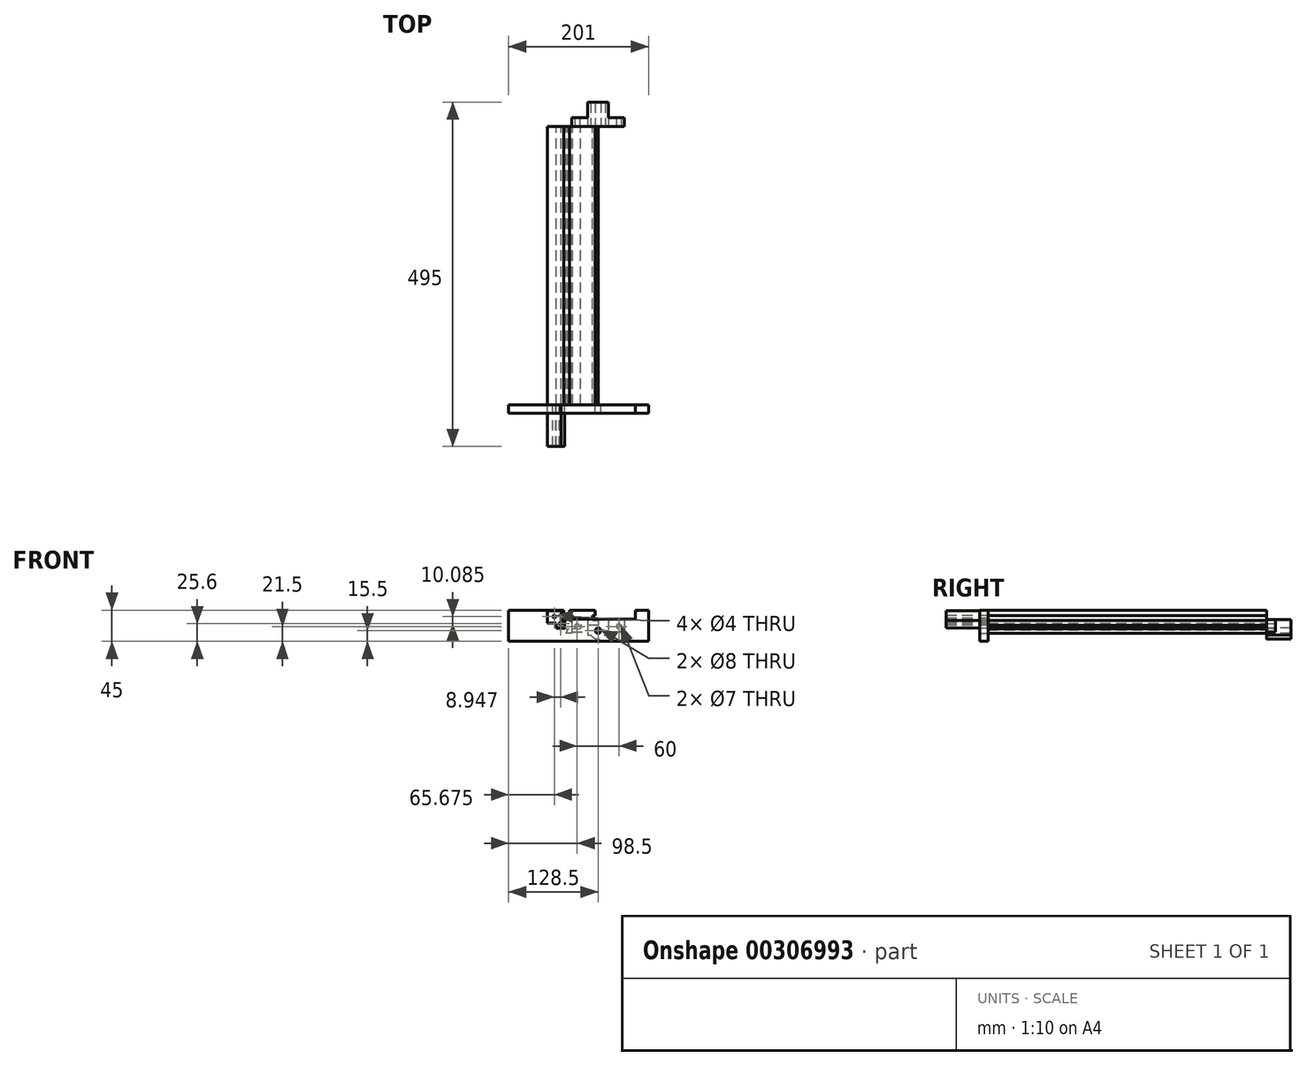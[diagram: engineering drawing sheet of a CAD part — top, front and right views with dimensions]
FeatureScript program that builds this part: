
annotation { "Feature Type Name" : "Feature", "Feature Type Description" : "" }
export const myFeature = defineFeature(function(context is Context, id is Id, definition is map)
    precondition{}
    {
        {
            var Q0;
            Q0=qCreatedBy(makeId("Front.planeOp"),FACE);
            var sketch = newSketch(context, id + "F0", { "sketchPlane" : qUnion([Q0])});
            skLineSegment(sketch, "E0", {"start": v(-4, 13.5) * mm, "end": v(-4, 5.5) * mm});
            skLineSegment(sketch, "E1", {"start": v(-4, 5.5) * mm, "end": v(-8.15, 5.5) * mm});
            skLineSegment(sketch, "E2", {"start": v(-8.15, 5.5) * mm, "end": v(-8.15, -1.5) * mm});
            skLineSegment(sketch, "E3", {"start": v(-8.15, -1.5) * mm, "end": v(0, -1.5) * mm});
            skLineSegment(sketch, "E4.MirrorCS", {"start": v(-45, 13.5) * mm, "end": v(-45, 30.96) * mm, "construction": true});
            skLineSegment(sketch, "E5.trimOffspring", {"start": v(-49, 13.5) * mm, "end": v(-72.5, 13.5) * mm});
            skLineSegment(sketch, "E6", {"start": v(-59.88, -5.13) * mm, "end": v(-59.88, -13.5) * mm});
            skLineSegment(sketch, "E7", {"start": v(-59.88, -13.5) * mm, "end": v(-43.75, -13.5) * mm});
            skLineSegment(sketch, "E8", {"start": v(-43.8, -14.95) * mm, "end": v(-46.06, -18.88) * mm});
            skLineSegment(sketch, "E9.0", {"start": v(-38.1, -19.88) * mm, "end": v(-46.06, -19.88) * mm});
            skLineSegment(sketch, "E10", {"start": v(-38.1, -13.32) * mm, "end": v(-38.1, -19.88) * mm});
            skLineSegment(sketch, "E11.MirrorCS", {"start": v(-43.75, -13.5) * mm, "end": v(-43.05, -12.8) * mm});
            skLineSegment(sketch, "E12.0", {"start": v(-43.8, -14.95) * mm, "end": v(-42.34, -13.5) * mm});
            skLineSegment(sketch, "E13", {"start": v(-42.34, -13.5) * mm, "end": v(-43.05, -12.8) * mm});
            skLineSegment(sketch, "E14", {"start": v(-46.06, -18.88) * mm, "end": v(-46.06, -19.88) * mm});
            skPoint(sketch, "E15.end.orphan", {"position": v(38.1, -8.38) * mm});
            skLineSegment(sketch, "E16", {"start": v(0, -8.5) * mm, "end": v(-25, -8.5) * mm});
            skLineSegment(sketch, "E17", {"start": v(-25, -8.5) * mm, "end": v(-25, -13.09) * mm});
            skLineSegment(sketch, "E18", {"start": v(-48.57, -13.5) * mm, "end": v(-42.45, -13.4) * mm, "construction": true});
            skLineSegment(sketch, "E19.trimOffspring", {"start": v(-38.1, -13.32) * mm, "end": v(-25, -13.09) * mm});
            skLineSegment(sketch, "E20.0", {"start": v(-49, -13.5) * mm, "end": v(-59.88, -13.5) * mm});
            skLineSegment(sketch, "E21", {"start": v(-72.5, 13.5) * mm, "end": v(-72.5, -5.13) * mm});
            skLineSegment(sketch, "E22", {"start": v(-72.5, -5.13) * mm, "end": v(-59.88, -5.13) * mm});
            skLineSegment(sketch, "E23.0.1.0", {"start": v(-53.15, -1.5) * mm, "end": v(-45, -1.5) * mm});
            skLineSegment(sketch, "E23.1.1.0", {"start": v(-49, 13.5) * mm, "end": v(-49, 5.5) * mm});
            skLineSegment(sketch, "E23.2.1.0", {"start": v(-49, 5.5) * mm, "end": v(-53.15, 5.5) * mm});
            skLineSegment(sketch, "E23.3.1.0", {"start": v(-53.15, 5.5) * mm, "end": v(-53.15, -1.5) * mm});
            skLineSegment(sketch, "E24.MirrorCS", {"start": v(-36.85, 5.5) * mm, "end": v(-36.85, -1.5) * mm});
            skLineSegment(sketch, "E25.MirrorCS", {"start": v(-41, 13.5) * mm, "end": v(-41, 5.5) * mm});
            skLineSegment(sketch, "E26.MirrorCS", {"start": v(-41, 5.5) * mm, "end": v(-36.85, 5.5) * mm});
            skLineSegment(sketch, "E27.MirrorCS", {"start": v(-36.85, -1.5) * mm, "end": v(-45, -1.5) * mm});
            skLineSegment(sketch, "E28", {"start": v(-41, 13.5) * mm, "end": v(-4, 13.5) * mm});
            skLineSegment(sketch, "E29", {"start": v(0, -1.5) * mm, "end": v(0, -8.5) * mm});
            skSolve(sketch);
        }
        {
            var Q0;
            Q0 = qSketchRegion(id + "F0", true);
            extrude(context, id + "F1", {"entities" : qUnion([Q0]), "endBound" : BoundingType.SYMMETRIC, "depth" : 400 * mm});
        }
        {
            var Q0;
            Q0=makeQuery(id+"F1.opExtrude","CAP_FACE",FACE,{"disambiguationData":[OSD([sQuery(id+"F0.wireOp",EDGE,"KvCxL1e1-7X7L-YcJv-dV07-MChgmQ6HNAH3.top"),sQuery(id+"F0.wireOp",EDGE,"KvCxL1e1-7X7L-YcJv-dV07-MChgmQ6HNAH3.left"),sQuery(id+"F0.wireOp",EDGE,"KvCxL1e1-7X7L-YcJv-dV07-MChgmQ6HNAH3.right"),sQuery(id+"F0.wireOp",EDGE,"E0"),sQuery(id+"F0.wireOp",EDGE,"E1"),sQuery(id+"F0.wireOp",EDGE,"E2"),sQuery(id+"F0.wireOp",EDGE,"E3"),sQuery(id+"F0.wireOp",EDGE,"RezQY5cE-oqyg-ECnA-D60h-5YGGmCgFMcgi"),sQuery(id+"F0.wireOp",EDGE,"5m8M1LIi-3tV8-qg0W-DIEx-wiA9uChcIzNi"),sQuery(id+"F0.wireOp",EDGE,"NXDqLafl-eDk5-Q1P5-A14y-Lj5f7TmusTVD"),sQuery(id+"F0.wireOp",EDGE,"d98be422-07de-4f6f-9fab-1498e4e71e56.trimOffspring"),sQuery(id+"F0.wireOp",EDGE,"94d0103f-7fe4-4f99-abae-38074f767762.1.0.0"),sQuery(id+"F0.wireOp",EDGE,"94d0103f-7fe4-4f99-abae-38074f767762.1.0.2"),sQuery(id+"F0.wireOp",EDGE,"94d0103f-7fe4-4f99-abae-38074f767762.1.0.3"),sQuery(id+"F0.wireOp",EDGE,"94d0103f-7fe4-4f99-abae-38074f767762.1.0.4"),sQuery(id+"F0.wireOp",EDGE,"94d0103f-7fe4-4f99-abae-38074f767762.1.0.5"),sQuery(id+"F0.wireOp",EDGE,"94d0103f-7fe4-4f99-abae-38074f767762.1.0.7"),sQuery(id+"F0.wireOp",EDGE,"94d0103f-7fe4-4f99-abae-38074f767762.1.0.8"),sQuery(id+"F0.wireOp",EDGE,"eeb253cc-f3de-4251-b503-4499be48a89b.trimOffspring"),sQuery(id+"F0.wireOp",EDGE,"38474f86-ac35-4713-8426-c426e6216f370.MirrorCS"),sQuery(id+"F0.wireOp",EDGE,"38474f86-ac35-4713-8426-c426e6216f371.MirrorCS"),sQuery(id+"F0.wireOp",EDGE,"38474f86-ac35-4713-8426-c426e6216f372.MirrorCS"),sQuery(id+"F0.wireOp",EDGE,"38474f86-ac35-4713-8426-c426e6216f373.MirrorCS"),sQuery(id+"F0.wireOp",EDGE,"38474f86-ac35-4713-8426-c426e6216f375.MirrorCS"),sQuery(id+"F0.wireOp",EDGE,"38474f86-ac35-4713-8426-c426e6216f376.MirrorCS"),sQuery(id+"F0.wireOp",EDGE,"38474f86-ac35-4713-8426-c426e6216f377.MirrorCS"),sQuery(id+"F0.wireOp",EDGE,"E5.trimOffspring"),sQuery(id+"F0.wireOp",EDGE,"8knJS9lv-uv0D-s0dx-EwQO-m9YQQ6HwGk3W"),sQuery(id+"F0.wireOp",EDGE,"E6"),sQuery(id+"F0.wireOp",EDGE,"VlTy60g8-z0oi-oBSS-4X3O-4UQM2Wkn6Heg"),sQuery(id+"F0.wireOp",EDGE,"oej1FxHs-by0u-Ded9-3bQH-CAGA97izaYjZ"),sQuery(id+"F0.wireOp",EDGE,"E7"),sQuery(id+"F0.wireOp",EDGE,"E8"),sQuery(id+"F0.wireOp",EDGE,"E9.0"),sQuery(id+"F0.wireOp",EDGE,"E10"),sQuery(id+"F0.wireOp",EDGE,"E11.MirrorCS"),sQuery(id+"F0.wireOp",EDGE,"E12.0"),sQuery(id+"F0.wireOp",EDGE,"E13"),sQuery(id+"F0.wireOp",EDGE,"E14"),sQuery(id+"F0.wireOp",EDGE,"0a26e11f-1d4c-405b-8192-a67988c49d7d0.MirrorCS"),sQuery(id+"F0.wireOp",EDGE,"0a26e11f-1d4c-405b-8192-a67988c49d7d1.MirrorCS"),sQuery(id+"F0.wireOp",EDGE,"0a26e11f-1d4c-405b-8192-a67988c49d7d2.MirrorCS"),sQuery(id+"F0.wireOp",EDGE,"0a26e11f-1d4c-405b-8192-a67988c49d7d3.MirrorCS"),sQuery(id+"F0.wireOp",EDGE,"0a26e11f-1d4c-405b-8192-a67988c49d7d4.MirrorCS"),sQuery(id+"F0.wireOp",EDGE,"0a26e11f-1d4c-405b-8192-a67988c49d7d5.MirrorCS"),sQuery(id+"F0.wireOp",EDGE,"0a26e11f-1d4c-405b-8192-a67988c49d7d6.MirrorCS"),sQuery(id+"F0.wireOp",EDGE,"0a26e11f-1d4c-405b-8192-a67988c49d7d7.MirrorCS"),sQuery(id+"F0.wireOp",EDGE,"E15")])],"isStart":false});
            var sketch = newSketch(context, id + "F2", { "sketchPlane" : qUnion([Q0])});
            skLineSegment(sketch, "E30.0", {"start": v(-72.5, -5.13) * mm, "end": v(-72.5, 13.5) * mm});
            skLineSegment(sketch, "E31.0", {"start": v(-72.5, -5.13) * mm, "end": v(-59.88, -5.13) * mm});
            skLineSegment(sketch, "E32.0", {"start": v(-59.88, -5.13) * mm, "end": v(-59.88, -12.3) * mm});
            skLineSegment(sketch, "E33.0", {"start": v(-59.88, -13.5) * mm, "end": v(-43.75, -13.5) * mm});
            skLineSegment(sketch, "E34", {"start": v(-72.5, 12.5) * mm, "end": v(-53.15, 12.5) * mm});
            skLineSegment(sketch, "E35", {"start": v(-53.15, 12.5) * mm, "end": v(-53.15, 0.5) * mm});
            skLineSegment(sketch, "E36", {"start": v(-53.15, 0.5) * mm, "end": v(-47.88, 0.5) * mm});
            skLineSegment(sketch, "E37", {"start": v(-47.88, 0.5) * mm, "end": v(-47.88, -12.3) * mm});
            skLineSegment(sketch, "E38", {"start": v(-59.88, -12.3) * mm, "end": v(-47.88, -12.3) * mm});
            skCircle(sketch, "E39", {"center": v(-62.82, 4.18) * mm, "radius": 2 * mm});
            skPoint(sketch, "E39.centerSnap0", {"position": v(-62.82, 12.5) * mm});
            skPoint(sketch, "E39.centerSnap1", {"position": v(-72.5, 4.18) * mm});
            skCircle(sketch, "E40", {"center": v(-53.88, -5.9) * mm, "radius": 2 * mm});
            skPoint(sketch, "E40.centerSnap0", {"position": v(-53.88, -12.3) * mm});
            skPoint(sketch, "E40.centerSnap1", {"position": v(-47.88, -5.9) * mm});
            skSolve(sketch);
        }
        {
            var Q0;
            {var subQ4=sQuery(id+"F2.wireOp",EDGE,"E31.0");Q0=makeQuery(id+"F2.imprint","IMPRINT",FACE,{"disambiguationData":[TD([[makeQuery(id+"F2.imprint","IMPRINT",EDGE,{"derivedFrom":subQ4}),1.0]])]});}
            extrude(context, id + "F3", {"entities" : qUnion([Q0]), "depth" : 60 * mm});
        }
        {
            var Q0;
            Q0=makeQuery(id+"F1.opExtrude","CAP_FACE",FACE,{"disambiguationData":[OSD([sQuery(id+"F0.wireOp",EDGE,"KvCxL1e1-7X7L-YcJv-dV07-MChgmQ6HNAH3.top"),sQuery(id+"F0.wireOp",EDGE,"KvCxL1e1-7X7L-YcJv-dV07-MChgmQ6HNAH3.left"),sQuery(id+"F0.wireOp",EDGE,"KvCxL1e1-7X7L-YcJv-dV07-MChgmQ6HNAH3.right"),sQuery(id+"F0.wireOp",EDGE,"E0"),sQuery(id+"F0.wireOp",EDGE,"E1"),sQuery(id+"F0.wireOp",EDGE,"E2"),sQuery(id+"F0.wireOp",EDGE,"E3"),sQuery(id+"F0.wireOp",EDGE,"RezQY5cE-oqyg-ECnA-D60h-5YGGmCgFMcgi"),sQuery(id+"F0.wireOp",EDGE,"5m8M1LIi-3tV8-qg0W-DIEx-wiA9uChcIzNi"),sQuery(id+"F0.wireOp",EDGE,"NXDqLafl-eDk5-Q1P5-A14y-Lj5f7TmusTVD"),sQuery(id+"F0.wireOp",EDGE,"d98be422-07de-4f6f-9fab-1498e4e71e56.trimOffspring"),sQuery(id+"F0.wireOp",EDGE,"94d0103f-7fe4-4f99-abae-38074f767762.1.0.0"),sQuery(id+"F0.wireOp",EDGE,"94d0103f-7fe4-4f99-abae-38074f767762.1.0.2"),sQuery(id+"F0.wireOp",EDGE,"94d0103f-7fe4-4f99-abae-38074f767762.1.0.3"),sQuery(id+"F0.wireOp",EDGE,"94d0103f-7fe4-4f99-abae-38074f767762.1.0.4"),sQuery(id+"F0.wireOp",EDGE,"94d0103f-7fe4-4f99-abae-38074f767762.1.0.5"),sQuery(id+"F0.wireOp",EDGE,"94d0103f-7fe4-4f99-abae-38074f767762.1.0.7"),sQuery(id+"F0.wireOp",EDGE,"94d0103f-7fe4-4f99-abae-38074f767762.1.0.8"),sQuery(id+"F0.wireOp",EDGE,"eeb253cc-f3de-4251-b503-4499be48a89b.trimOffspring"),sQuery(id+"F0.wireOp",EDGE,"38474f86-ac35-4713-8426-c426e6216f370.MirrorCS"),sQuery(id+"F0.wireOp",EDGE,"38474f86-ac35-4713-8426-c426e6216f371.MirrorCS"),sQuery(id+"F0.wireOp",EDGE,"38474f86-ac35-4713-8426-c426e6216f372.MirrorCS"),sQuery(id+"F0.wireOp",EDGE,"38474f86-ac35-4713-8426-c426e6216f373.MirrorCS"),sQuery(id+"F0.wireOp",EDGE,"38474f86-ac35-4713-8426-c426e6216f375.MirrorCS"),sQuery(id+"F0.wireOp",EDGE,"38474f86-ac35-4713-8426-c426e6216f376.MirrorCS"),sQuery(id+"F0.wireOp",EDGE,"38474f86-ac35-4713-8426-c426e6216f377.MirrorCS"),sQuery(id+"F0.wireOp",EDGE,"E5.trimOffspring"),sQuery(id+"F0.wireOp",EDGE,"8knJS9lv-uv0D-s0dx-EwQO-m9YQQ6HwGk3W"),sQuery(id+"F0.wireOp",EDGE,"E6"),sQuery(id+"F0.wireOp",EDGE,"VlTy60g8-z0oi-oBSS-4X3O-4UQM2Wkn6Heg"),sQuery(id+"F0.wireOp",EDGE,"oej1FxHs-by0u-Ded9-3bQH-CAGA97izaYjZ"),sQuery(id+"F0.wireOp",EDGE,"E7"),sQuery(id+"F0.wireOp",EDGE,"E8"),sQuery(id+"F0.wireOp",EDGE,"E9.0"),sQuery(id+"F0.wireOp",EDGE,"E10"),sQuery(id+"F0.wireOp",EDGE,"E11.MirrorCS"),sQuery(id+"F0.wireOp",EDGE,"E12.0"),sQuery(id+"F0.wireOp",EDGE,"E13"),sQuery(id+"F0.wireOp",EDGE,"E14"),sQuery(id+"F0.wireOp",EDGE,"0a26e11f-1d4c-405b-8192-a67988c49d7d0.MirrorCS"),sQuery(id+"F0.wireOp",EDGE,"0a26e11f-1d4c-405b-8192-a67988c49d7d1.MirrorCS"),sQuery(id+"F0.wireOp",EDGE,"0a26e11f-1d4c-405b-8192-a67988c49d7d2.MirrorCS"),sQuery(id+"F0.wireOp",EDGE,"0a26e11f-1d4c-405b-8192-a67988c49d7d3.MirrorCS"),sQuery(id+"F0.wireOp",EDGE,"0a26e11f-1d4c-405b-8192-a67988c49d7d4.MirrorCS"),sQuery(id+"F0.wireOp",EDGE,"0a26e11f-1d4c-405b-8192-a67988c49d7d5.MirrorCS"),sQuery(id+"F0.wireOp",EDGE,"0a26e11f-1d4c-405b-8192-a67988c49d7d6.MirrorCS"),sQuery(id+"F0.wireOp",EDGE,"0a26e11f-1d4c-405b-8192-a67988c49d7d7.MirrorCS"),sQuery(id+"F0.wireOp",EDGE,"E15")])],"isStart":true});
            var sketch = newSketch(context, id + "F4", { "sketchPlane" : qUnion([Q0])});
            skLineSegment(sketch, "E41.0", {"start": v(8.15, -2) * mm, "end": v(-8.15, -1.99) * mm, "construction": true});
            skLineSegment(sketch, "E42", {"start": v(0, 0) * mm, "end": v(0, -27.32) * mm, "construction": true});
            skLineSegment(sketch, "E43", {"start": v(0, 0) * mm, "end": v(37.5, -0.03) * mm});
            skLineSegment(sketch, "E44", {"start": v(37.5, -0.03) * mm, "end": v(37.5, -18.03) * mm});
            skLineSegment(sketch, "E45", {"start": v(37.5, -18.03) * mm, "end": v(15, -18.03) * mm});
            skLineSegment(sketch, "E46", {"start": v(15, -18.03) * mm, "end": v(15, -22.03) * mm});
            skLineSegment(sketch, "E47", {"start": v(15, -22.03) * mm, "end": v(10.38, -22.03) * mm});
            skPoint(sketch, "E48", {"position": v(30, -10) * mm});
            skLineSegment(sketch, "E49.MirrorCS", {"start": v(0, 0) * mm, "end": v(-37.5, -0.03) * mm});
            skLineSegment(sketch, "E50.MirrorCS", {"start": v(-37.5, -0.03) * mm, "end": v(-37.5, -18.03) * mm});
            skLineSegment(sketch, "E51.MirrorCS", {"start": v(-37.5, -18.03) * mm, "end": v(-15, -18.03) * mm});
            skLineSegment(sketch, "E52.MirrorCS", {"start": v(-15, -18.03) * mm, "end": v(-15, -22.03) * mm});
            skLineSegment(sketch, "E53.MirrorCS", {"start": v(-15, -22.03) * mm, "end": v(-10.38, -22.03) * mm});
            skPoint(sketch, "E54.MirrorP", {"position": v(-30, -10) * mm});
            skCircle(sketch, "E55", {"center": v(30, -10) * mm, "radius": 3.5 * mm});
            skCircle(sketch, "E56", {"center": v(0, -16) * mm, "radius": 4 * mm});
            skArc(sketch, "E57", {"start": v(-10.38, -22.03) * mm, "mid": v(0, -28) * mm, "end": v(10.38, -22.03) * mm});
            skPoint(sketch, "E58.orphan", {"position": v(0, -22.03) * mm});
            skCircle(sketch, "E59.MirrorC", {"center": v(-30, -10) * mm, "radius": 3.5 * mm});
            skSolve(sketch);
        }
        {
            var Q0;
            Q0 = qSketchRegion(id + "F4", true);
            extrude(context, id + "F5", {"entities" : qUnion([Q0]), "depth" : 13 * mm, "offsetDistance" : 25 * mm});
        }
        {
            var Q0;
            Q0=makeQuery(id+"F5.opExtrude","CAP_FACE",FACE,{"disambiguationData":[OSD([sQuery(id+"F4.wireOp",EDGE,"E43"),sQuery(id+"F4.wireOp",EDGE,"E44"),sQuery(id+"F4.wireOp",EDGE,"E45"),sQuery(id+"F4.wireOp",EDGE,"E46"),sQuery(id+"F4.wireOp",EDGE,"E47"),sQuery(id+"F4.wireOp",EDGE,"E49.MirrorCS"),sQuery(id+"F4.wireOp",EDGE,"E50.MirrorCS"),sQuery(id+"F4.wireOp",EDGE,"E51.MirrorCS"),sQuery(id+"F4.wireOp",EDGE,"E52.MirrorCS"),sQuery(id+"F4.wireOp",EDGE,"E53.MirrorCS"),sQuery(id+"F4.wireOp",EDGE,"E55"),sQuery(id+"F4.wireOp",EDGE,"E56"),sQuery(id+"F4.wireOp",EDGE,"E57"),sQuery(id+"F4.wireOp",EDGE,"E59.MirrorC")])],"isStart":false});
            var sketch = newSketch(context, id + "F6", { "sketchPlane" : qUnion([Q0])});
            skLineSegment(sketch, "E60", {"start": v(15, -22.03) * mm, "end": v(15, -0.01) * mm});
            skLineSegment(sketch, "E61", {"start": v(15, -0.01) * mm, "end": v(-15, 0.01) * mm});
            skLineSegment(sketch, "E62", {"start": v(-15, 0.01) * mm, "end": v(-15, -22.03) * mm});
            skLineSegment(sketch, "E63", {"start": v(-15, -22.03) * mm, "end": v(-10.38, -22.03) * mm});
            skSolve(sketch);
        }
        {
            var Q0;
            {var subQ2=sQuery(id+"F6.wireOp",EDGE,"E61");Q0=makeQuery(id+"F6.imprint","IMPRINT",FACE,{"disambiguationData":[TD([[makeQuery(id+"F6.imprint","IMPRINT",EDGE,{"derivedFrom":subQ2}),-1.0]])]});}
            extrude(context, id + "F7", {"entities" : qUnion([Q0]), "operationType" : NewBodyOperationType.ADD, "depth" : 22 * mm, "offsetDistance" : 25 * mm});
        }
        {
            var Q0;
            Q0=makeQuery(id+"F1.opExtrude","CAP_FACE",FACE,{"disambiguationData":[OSD([sQuery(id+"F0.wireOp",EDGE,"KvCxL1e1-7X7L-YcJv-dV07-MChgmQ6HNAH3.top"),sQuery(id+"F0.wireOp",EDGE,"KvCxL1e1-7X7L-YcJv-dV07-MChgmQ6HNAH3.left"),sQuery(id+"F0.wireOp",EDGE,"KvCxL1e1-7X7L-YcJv-dV07-MChgmQ6HNAH3.right"),sQuery(id+"F0.wireOp",EDGE,"E0"),sQuery(id+"F0.wireOp",EDGE,"E1"),sQuery(id+"F0.wireOp",EDGE,"E2"),sQuery(id+"F0.wireOp",EDGE,"E3"),sQuery(id+"F0.wireOp",EDGE,"RezQY5cE-oqyg-ECnA-D60h-5YGGmCgFMcgi"),sQuery(id+"F0.wireOp",EDGE,"5m8M1LIi-3tV8-qg0W-DIEx-wiA9uChcIzNi"),sQuery(id+"F0.wireOp",EDGE,"NXDqLafl-eDk5-Q1P5-A14y-Lj5f7TmusTVD"),sQuery(id+"F0.wireOp",EDGE,"d98be422-07de-4f6f-9fab-1498e4e71e56.trimOffspring"),sQuery(id+"F0.wireOp",EDGE,"94d0103f-7fe4-4f99-abae-38074f767762.1.0.0"),sQuery(id+"F0.wireOp",EDGE,"94d0103f-7fe4-4f99-abae-38074f767762.1.0.2"),sQuery(id+"F0.wireOp",EDGE,"94d0103f-7fe4-4f99-abae-38074f767762.1.0.3"),sQuery(id+"F0.wireOp",EDGE,"94d0103f-7fe4-4f99-abae-38074f767762.1.0.4"),sQuery(id+"F0.wireOp",EDGE,"94d0103f-7fe4-4f99-abae-38074f767762.1.0.5"),sQuery(id+"F0.wireOp",EDGE,"94d0103f-7fe4-4f99-abae-38074f767762.1.0.7"),sQuery(id+"F0.wireOp",EDGE,"94d0103f-7fe4-4f99-abae-38074f767762.1.0.8"),sQuery(id+"F0.wireOp",EDGE,"eeb253cc-f3de-4251-b503-4499be48a89b.trimOffspring"),sQuery(id+"F0.wireOp",EDGE,"38474f86-ac35-4713-8426-c426e6216f370.MirrorCS"),sQuery(id+"F0.wireOp",EDGE,"38474f86-ac35-4713-8426-c426e6216f371.MirrorCS"),sQuery(id+"F0.wireOp",EDGE,"38474f86-ac35-4713-8426-c426e6216f372.MirrorCS"),sQuery(id+"F0.wireOp",EDGE,"38474f86-ac35-4713-8426-c426e6216f373.MirrorCS"),sQuery(id+"F0.wireOp",EDGE,"38474f86-ac35-4713-8426-c426e6216f375.MirrorCS"),sQuery(id+"F0.wireOp",EDGE,"38474f86-ac35-4713-8426-c426e6216f376.MirrorCS"),sQuery(id+"F0.wireOp",EDGE,"38474f86-ac35-4713-8426-c426e6216f377.MirrorCS"),sQuery(id+"F0.wireOp",EDGE,"E5.trimOffspring"),sQuery(id+"F0.wireOp",EDGE,"8knJS9lv-uv0D-s0dx-EwQO-m9YQQ6HwGk3W"),sQuery(id+"F0.wireOp",EDGE,"E6"),sQuery(id+"F0.wireOp",EDGE,"VlTy60g8-z0oi-oBSS-4X3O-4UQM2Wkn6Heg"),sQuery(id+"F0.wireOp",EDGE,"oej1FxHs-by0u-Ded9-3bQH-CAGA97izaYjZ"),sQuery(id+"F0.wireOp",EDGE,"E7"),sQuery(id+"F0.wireOp",EDGE,"E8"),sQuery(id+"F0.wireOp",EDGE,"E9.0"),sQuery(id+"F0.wireOp",EDGE,"E10"),sQuery(id+"F0.wireOp",EDGE,"E11.MirrorCS"),sQuery(id+"F0.wireOp",EDGE,"E12.0"),sQuery(id+"F0.wireOp",EDGE,"E13"),sQuery(id+"F0.wireOp",EDGE,"E14"),sQuery(id+"F0.wireOp",EDGE,"0a26e11f-1d4c-405b-8192-a67988c49d7d0.MirrorCS"),sQuery(id+"F0.wireOp",EDGE,"0a26e11f-1d4c-405b-8192-a67988c49d7d1.MirrorCS"),sQuery(id+"F0.wireOp",EDGE,"0a26e11f-1d4c-405b-8192-a67988c49d7d2.MirrorCS"),sQuery(id+"F0.wireOp",EDGE,"0a26e11f-1d4c-405b-8192-a67988c49d7d3.MirrorCS"),sQuery(id+"F0.wireOp",EDGE,"0a26e11f-1d4c-405b-8192-a67988c49d7d4.MirrorCS"),sQuery(id+"F0.wireOp",EDGE,"0a26e11f-1d4c-405b-8192-a67988c49d7d5.MirrorCS"),sQuery(id+"F0.wireOp",EDGE,"0a26e11f-1d4c-405b-8192-a67988c49d7d6.MirrorCS"),sQuery(id+"F0.wireOp",EDGE,"0a26e11f-1d4c-405b-8192-a67988c49d7d7.MirrorCS"),sQuery(id+"F0.wireOp",EDGE,"E15")])],"isStart":false});
            var sketch = newSketch(context, id + "F8", { "sketchPlane" : qUnion([Q0])});
            skLineSegment(sketch, "E64", {"start": v(72.5, 13.5) * mm, "end": v(53.5, 13.5) * mm});
            skLineSegment(sketch, "E65", {"start": v(53.5, 13.5) * mm, "end": v(53.5, 0.5) * mm});
            skLineSegment(sketch, "E66", {"start": v(53.5, 0.5) * mm, "end": v(-54, 0.5) * mm});
            skLineSegment(sketch, "E67", {"start": v(-54, 0.5) * mm, "end": v(-54, 13.5) * mm});
            skLineSegment(sketch, "E68", {"start": v(-54, 13.5) * mm, "end": v(-128.5, 13.5) * mm});
            skLineSegment(sketch, "E69", {"start": v(-128.5, 13.5) * mm, "end": v(-128.5, -31.5) * mm});
            skLineSegment(sketch, "E70", {"start": v(-128.5, -31.5) * mm, "end": v(72.5, -31.5) * mm});
            skLineSegment(sketch, "E71", {"start": v(72.5, -31.5) * mm, "end": v(72.5, 13.5) * mm});
            skCircle(sketch, "E72.0", {"center": v(-62.82, 4.18) * mm, "radius": 2 * mm});
            skCircle(sketch, "E73.0", {"center": v(-53.88, -5.9) * mm, "radius": 2 * mm});
            skCircle(sketch, "E74.0", {"center": v(0, -16) * mm, "radius": 4 * mm});
            skSolve(sketch);
        }
        {
            var Q0;
            Q0 = qSketchRegion(id + "F8", true);
            extrude(context, id + "F9", {"entities" : qUnion([Q0]), "depth" : 12 * mm, "offsetDistance" : 25 * mm});
        }
    });
